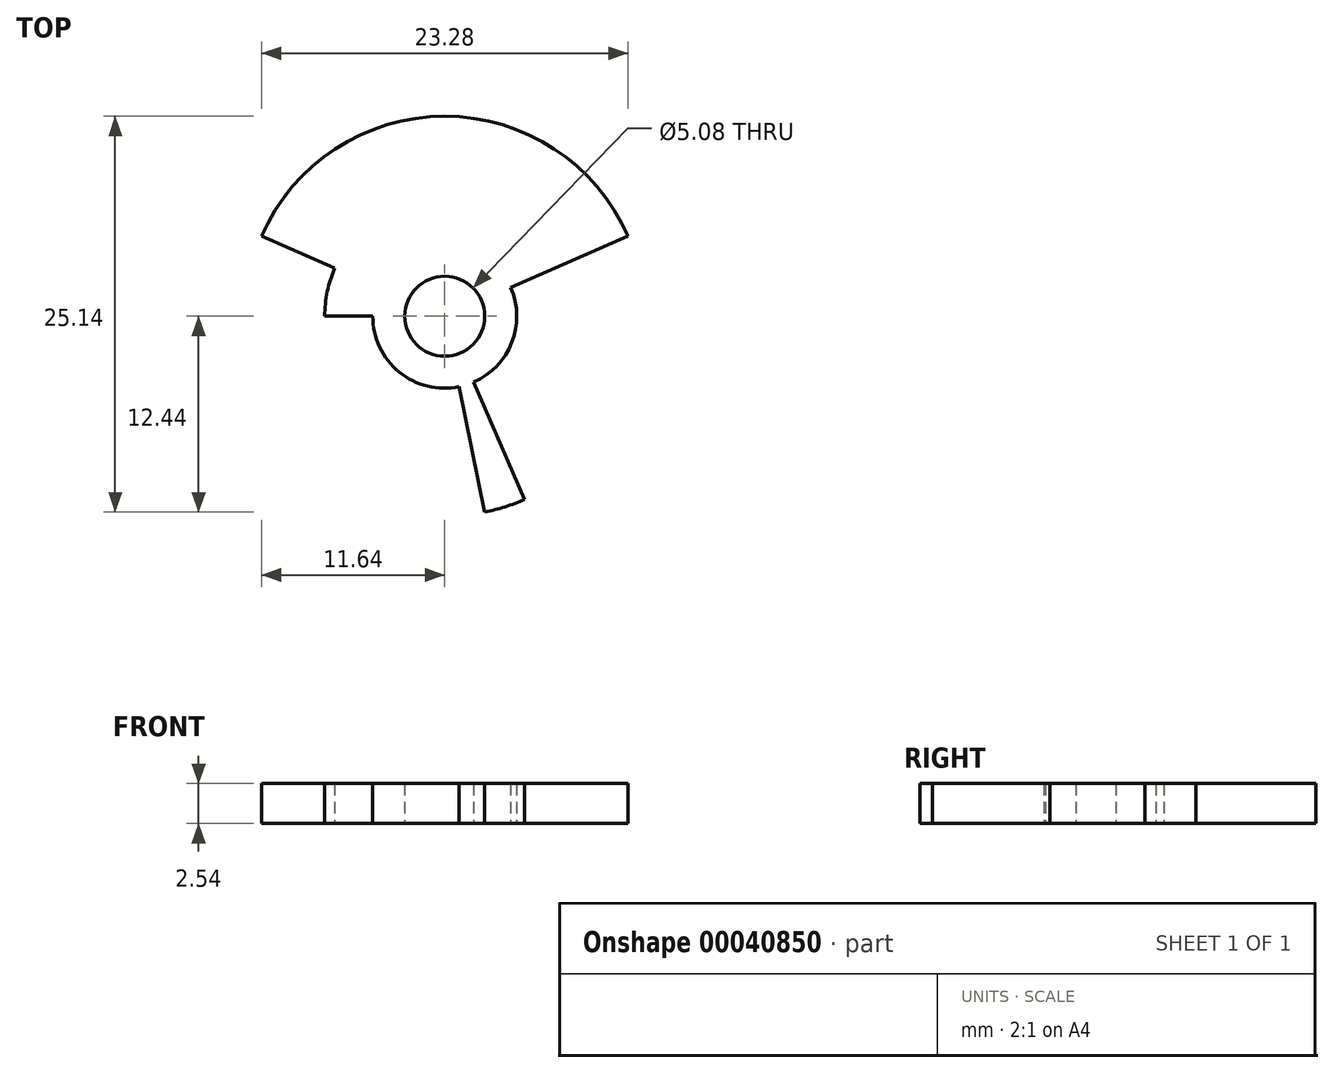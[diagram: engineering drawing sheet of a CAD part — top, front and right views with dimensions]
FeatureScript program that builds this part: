
annotation { "Feature Type Name" : "Feature", "Feature Type Description" : "" }
export const myFeature = defineFeature(function(context is Context, id is Id, definition is map)
    precondition{}
    {
        {
            var Q0;
            Q0=qCreatedBy(makeId("Top.planeOp"),FACE);
            var sketch = newSketch(context, id + "F0", { "sketchPlane" : qUnion([Q0])});
            skLineSegment(sketch, "E0", {"start": v(0, 0) * mm, "end": v(12.7, 0) * mm});
            skCircle(sketch, "E1", {"center": v(0, 0) * mm, "radius": 12.7 * mm});
            skLineSegment(sketch, "E2", {"start": v(0, 0) * mm, "end": v(7.62, 0) * mm});
            skLineSegment(sketch, "E3", {"start": v(0, 0) * mm, "end": v(2.54, 0) * mm});
            skCircle(sketch, "E4", {"center": v(0, 0) * mm, "radius": 7.62 * mm});
            skCircle(sketch, "E5", {"center": v(0, 0) * mm, "radius": 2.54 * mm});
            skLineSegment(sketch, "E6", {"start": v(0, 0) * mm, "end": v(4.57, 0) * mm});
            skCircle(sketch, "E7", {"center": v(0, 0) * mm, "radius": 4.57 * mm});
            skLineSegment(sketch, "E8", {"start": v(0, 0) * mm, "end": v(11.64, 5.08) * mm});
            skLineSegment(sketch, "E9", {"start": v(0, 0) * mm, "end": v(-11.64, 5.08) * mm});
            skLineSegment(sketch, "E10", {"start": v(0, 0) * mm, "end": v(2.54, -12.44) * mm});
            skLineSegment(sketch, "E11", {"start": v(0, 0) * mm, "end": v(5.08, -11.64) * mm});
            skLineSegment(sketch, "E12", {"start": v(0, 0) * mm, "end": v(-12.7, 0) * mm});
            skSolve(sketch);
        }
        {
            var Q0;
            {var subQ3=sQuery(id+"F0.wireOp",EDGE,"E1");var subQ5=sQuery(id+"F0.wireOp",EDGE,"E8");var subQ7=makeQuery(id+"F0.imprint","INTERSECT",VERTEX,{"derivedFrom":[subQ3,subQ5]});Q0=makeQuery(id+"F0.imprint","IMPRINT",FACE,{"disambiguationData":[TD([[makeQuery(id+"F0.imprint","IMPRINT",EDGE,{"disambiguationData":[TD([[subQ7,-1.0]])],"derivedFrom":subQ3}),1.0]])]});}
            var Q1;
            {var subQ3=sQuery(id+"F0.wireOp",EDGE,"E4");var subQ5=sQuery(id+"F0.wireOp",EDGE,"E8");var subQ7=makeQuery(id+"F0.imprint","INTERSECT",VERTEX,{"derivedFrom":[subQ3,subQ5]});Q1=makeQuery(id+"F0.imprint","IMPRINT",FACE,{"disambiguationData":[TD([[makeQuery(id+"F0.imprint","IMPRINT",EDGE,{"disambiguationData":[TD([[subQ7,-1.0]])],"derivedFrom":subQ3}),1.0]])]});}
            var Q2;
            {var subQ3=sQuery(id+"F0.wireOp",EDGE,"E4");var subQ5=sQuery(id+"F0.wireOp",EDGE,"E9");var subQ7=makeQuery(id+"F0.imprint","INTERSECT",VERTEX,{"derivedFrom":[subQ3,subQ5]});Q2=makeQuery(id+"F0.imprint","IMPRINT",FACE,{"disambiguationData":[TD([[makeQuery(id+"F0.imprint","IMPRINT",EDGE,{"disambiguationData":[TD([[subQ7,-1.0]])],"derivedFrom":subQ3}),1.0]])]});}
            var Q3;
            {var subQ5=sQuery(id+"F0.wireOp",EDGE,"E2");Q3=makeQuery(id+"F0.imprint","IMPRINT",FACE,{"disambiguationData":[TD([[makeQuery(id+"F0.imprint","IMPRINT",EDGE,{"derivedFrom":subQ5}),1.0]])]});}
            var Q4;
            {var subQ3=sQuery(id+"F0.wireOp",EDGE,"E5");var subQ5=sQuery(id+"F0.wireOp",EDGE,"E8");var subQ7=makeQuery(id+"F0.imprint","INTERSECT",VERTEX,{"derivedFrom":[subQ3,subQ5]});Q4=makeQuery(id+"F0.imprint","IMPRINT",FACE,{"disambiguationData":[TD([[makeQuery(id+"F0.imprint","IMPRINT",EDGE,{"disambiguationData":[TD([[subQ7,-1.0]])],"derivedFrom":subQ3}),-1.0]])]});}
            var Q5;
            {var subQ3=sQuery(id+"F0.wireOp",EDGE,"E5");var subQ5=sQuery(id+"F0.wireOp",EDGE,"E9");var subQ7=makeQuery(id+"F0.imprint","INTERSECT",VERTEX,{"derivedFrom":[subQ3,subQ5]});Q5=makeQuery(id+"F0.imprint","IMPRINT",FACE,{"disambiguationData":[TD([[makeQuery(id+"F0.imprint","IMPRINT",EDGE,{"disambiguationData":[TD([[subQ7,-1.0]])],"derivedFrom":subQ3}),-1.0]])]});}
            var Q6;
            {var subQ1=sQuery(id+"F0.wireOp",EDGE,"E8");var subQ5=sQuery(id+"F0.wireOp",EDGE,"E5");var subQ7=makeQuery(id+"F0.imprint","INTERSECT",VERTEX,{"derivedFrom":[subQ5,subQ1]});Q6=makeQuery(id+"F0.imprint","IMPRINT",FACE,{"disambiguationData":[TD([[makeQuery(id+"F0.imprint","IMPRINT",EDGE,{"disambiguationData":[TD([[subQ7,1.0]])],"derivedFrom":subQ5}),-1.0]])]});}
            var Q7;
            {var subQ0=sQuery(id+"F0.wireOp",EDGE,"E12");var subQ3=sQuery(id+"F0.wireOp",EDGE,"E5");var subQ4=makeQuery(id+"F0.imprint","INTERSECT",VERTEX,{"derivedFrom":[subQ3,subQ0]});Q7=makeQuery(id+"F0.imprint","IMPRINT",FACE,{"disambiguationData":[TD([[makeQuery(id+"F0.imprint","IMPRINT",EDGE,{"disambiguationData":[TD([[subQ4,-1.0]])],"derivedFrom":subQ3}),-1.0]])]});}
            var Q8;
            {var subQ0=sQuery(id+"F0.wireOp",EDGE,"E10");var subQ3=sQuery(id+"F0.wireOp",EDGE,"E5");var subQ4=makeQuery(id+"F0.imprint","INTERSECT",VERTEX,{"derivedFrom":[subQ3,subQ0]});Q8=makeQuery(id+"F0.imprint","IMPRINT",FACE,{"disambiguationData":[TD([[makeQuery(id+"F0.imprint","IMPRINT",EDGE,{"disambiguationData":[TD([[subQ4,-1.0]])],"derivedFrom":subQ3}),-1.0]])]});}
            var Q9;
            {var subQ3=sQuery(id+"F0.wireOp",EDGE,"E5");var subQ5=sQuery(id+"F0.wireOp",EDGE,"E6");var subQ7=makeQuery(id+"F0.imprint","INTERSECT",VERTEX,{"derivedFrom":[subQ3,subQ5]});Q9=makeQuery(id+"F0.imprint","IMPRINT",FACE,{"disambiguationData":[TD([[makeQuery(id+"F0.imprint","IMPRINT",EDGE,{"disambiguationData":[TD([[subQ7,1.0]])],"derivedFrom":subQ3}),-1.0]])]});}
            var Q10;
            {var subQ0=sQuery(id+"F0.wireOp",EDGE,"E10");var subQ3=sQuery(id+"F0.wireOp",EDGE,"E1");var subQ4=makeQuery(id+"F0.imprint","INTERSECT",VERTEX,{"derivedFrom":[subQ3,subQ0]});Q10=makeQuery(id+"F0.imprint","IMPRINT",FACE,{"disambiguationData":[TD([[makeQuery(id+"F0.imprint","IMPRINT",EDGE,{"disambiguationData":[TD([[subQ4,-1.0]])],"derivedFrom":subQ3}),1.0]])]});}
            var Q11;
            {var subQ0=sQuery(id+"F0.wireOp",EDGE,"E10");var subQ3=sQuery(id+"F0.wireOp",EDGE,"E4");var subQ4=makeQuery(id+"F0.imprint","INTERSECT",VERTEX,{"derivedFrom":[subQ3,subQ0]});Q11=makeQuery(id+"F0.imprint","IMPRINT",FACE,{"disambiguationData":[TD([[makeQuery(id+"F0.imprint","IMPRINT",EDGE,{"disambiguationData":[TD([[subQ4,-1.0]])],"derivedFrom":subQ3}),1.0]])]});}
            extrude(context, id + "F1", {"entities" : qUnion([Q0, Q1, Q2, Q3, Q4, Q5, Q6, Q7, Q8, Q9, Q10, Q11]), "depth" : 2.54 * mm});
        }
    });
